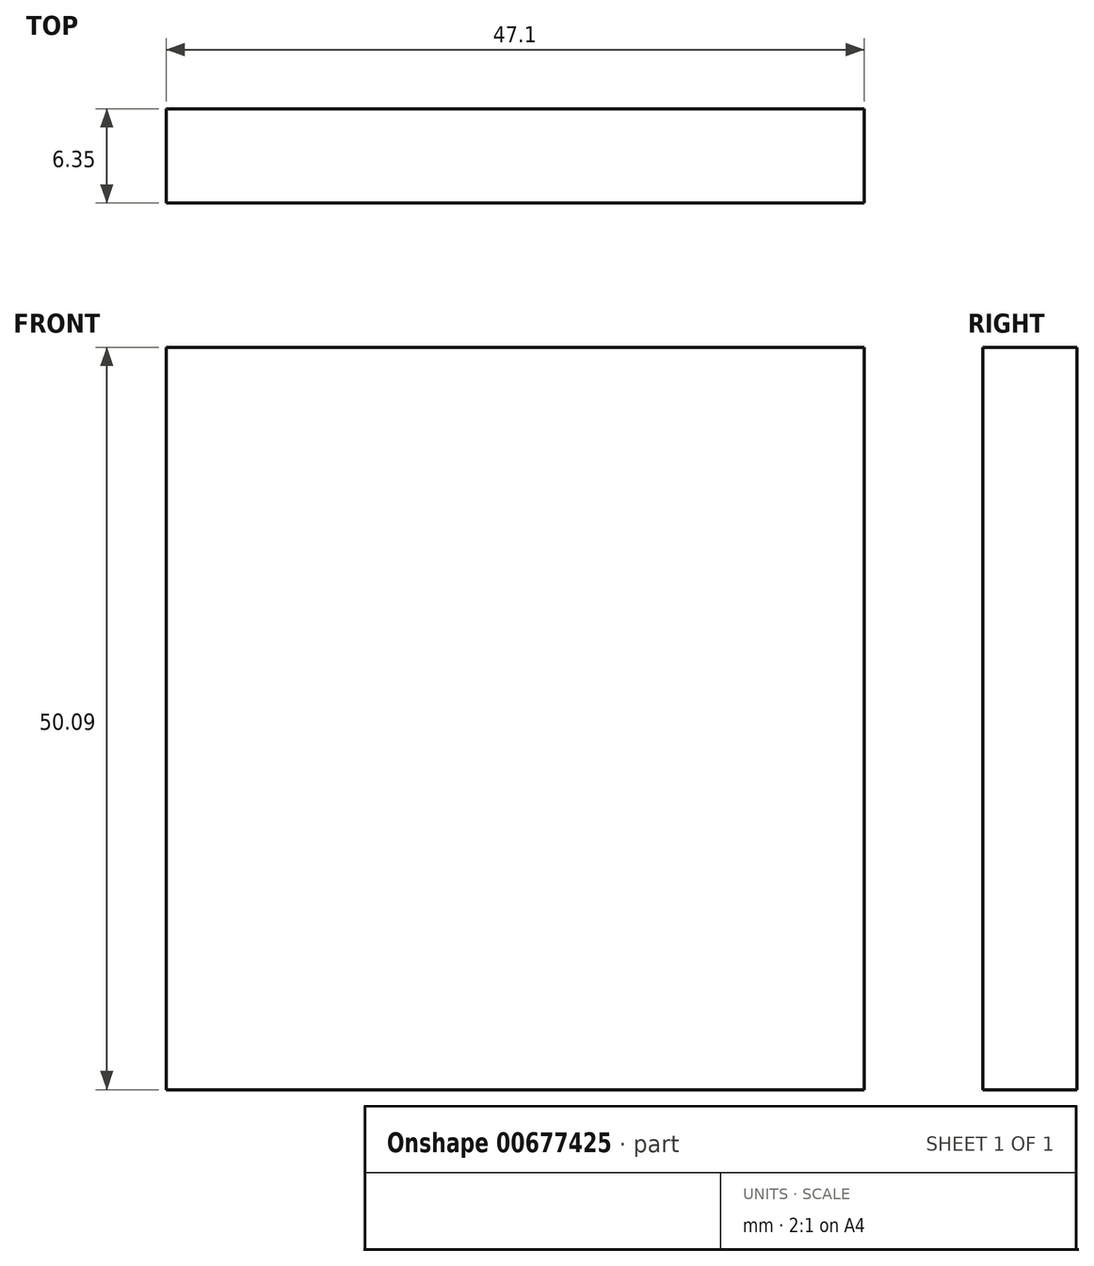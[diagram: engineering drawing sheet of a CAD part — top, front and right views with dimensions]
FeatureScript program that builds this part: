
annotation { "Feature Type Name" : "Feature", "Feature Type Description" : "" }
export const myFeature = defineFeature(function(context is Context, id is Id, definition is map)
    precondition{}
    {
        {
            var Q0;
            Q0=qCreatedBy(makeId("Front.planeOp"),FACE);
            var sketch = newSketch(context, id + "F0", { "sketchPlane" : qUnion([Q0])});
            skLineSegment(sketch, "E0.bottom", {"start": v(-25.38, 49.64) * mm, "end": v(21.72, 49.64) * mm});
            skLineSegment(sketch, "E0.top", {"start": v(-25.38, -0.45) * mm, "end": v(21.72, -0.45) * mm});
            skLineSegment(sketch, "E0.left", {"start": v(-25.38, 49.64) * mm, "end": v(-25.38, -0.45) * mm});
            skLineSegment(sketch, "E0.right", {"start": v(21.72, 49.64) * mm, "end": v(21.72, -0.45) * mm});
            skSolve(sketch);
        }
        {
            var Q0;
            Q0=makeQuery(id+"F0.imprint","IMPRINT",FACE,{"disambiguationData":[TD([[makeQuery(id+"F0.imprint","IMPRINT",EDGE,{"derivedFrom":sQuery(id+"F0.wireOp",EDGE,"E0.bottom")}),-1.0]])]});
            extrude(context, id + "F1", {"entities" : qUnion([Q0]), "depth" : 6.35 * mm, "offsetDistance" : 25.4 * mm});
        }
    });
